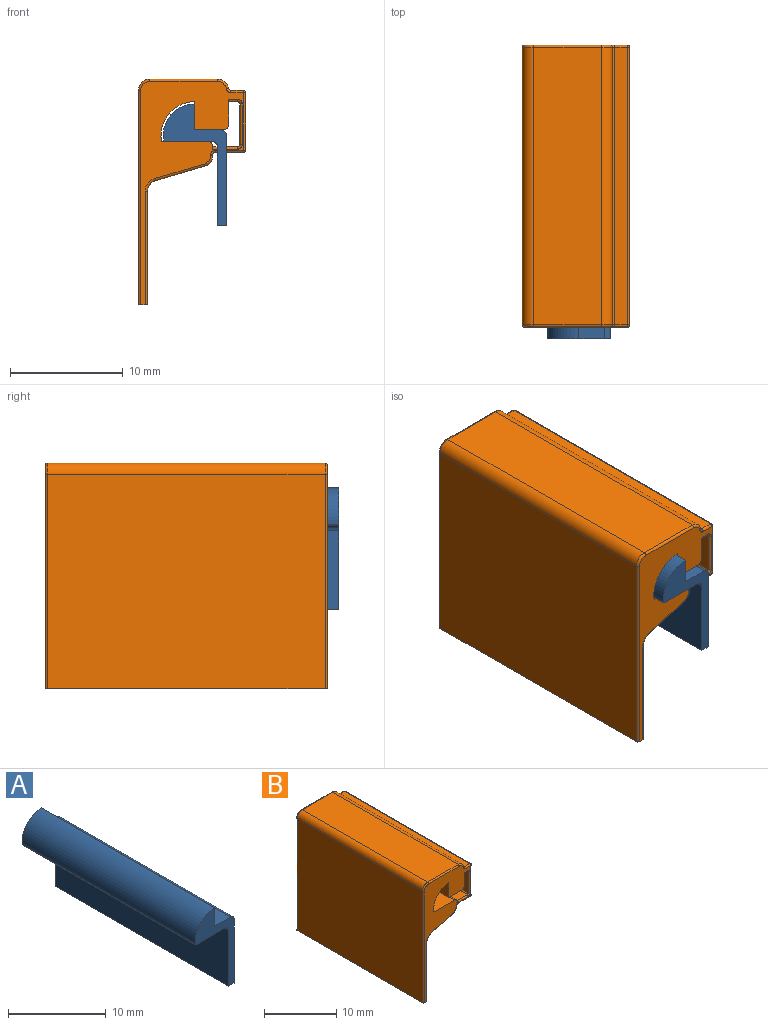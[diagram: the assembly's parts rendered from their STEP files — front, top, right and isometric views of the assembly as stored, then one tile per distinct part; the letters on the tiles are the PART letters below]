
ASSEMBLY  parts=2 mates=1
PART A: 12 faces, bbox 5.6x25x10.8 mm
  f0: plane 25x4.17mm, normal (0,0,-1), area 104.3mm2, adj f1,f9,f10,f11
  f1: cylinder r=0.5mm len=25mm, axis (0,1,0), area 19.6mm2, adj f0,f2,f10,f11
  f2: plane 25x7mm, normal (-1,0,0), area 175mm2, adj f1,f3,f10,f11
  f3: plane 25x0.8mm, normal (0,0,-1), area 20mm2, adj f2,f4,f10,f11
  f4: plane 25x8mm, normal (1,0,0), area 200mm2, adj f3,f5,f10,f11
  f5: cylinder r=0.5mm len=25mm, axis (0,1,0), area 19.6mm2, adj f4,f6,f10,f11
  f6: plane 25x2.3mm, normal (0,0,1), area 57.5mm2, adj f5,f7,f10,f11
  f7: plane 25x2.3mm, normal (1,0,0), area 57.5mm2, adj f6,f8,f10,f11
  f8: cylinder r=2.8mm len=25mm, axis (0,1,0), area 120.4mm2, adj f7,f9,f10,f11
  f9: cylinder r=0.1mm len=25mm, axis (0,1,0), area 3.6mm2, adj f0,f8,f10,f11
  f10: plane 10.8x5.6mm, normal (0,-1,0), area 16.3mm2, adj f0,f1,f2,f3,f4,f5,f6,f7
  f11: plane 10.8x5.6mm, normal (0,1,0), area 16.3mm2, adj f0,f1,f2,f3,f4,f5,f6,f7
PART B: 74 faces, bbox 9.6x25x20.1 mm
  f0: plane 25x2.2mm, normal (1,0,0), area 50mm2, adj f12,f13,f18,f24,f64,f73
  f1: plane 25x3.97mm, normal (0,0,1), area 99.3mm2, adj f2,f12,f13,f19
  f2: cylinder r=0.1mm len=25mm, axis (0,1,0), area 3.6mm2, adj f1,f3,f12,f13
  f3: cylinder r=3mm len=25mm, axis (0,1,0), area 128.2mm2, adj f2,f4,f12,f13
  f4: plane 25x2.5mm, normal (-1,0,0), area 62.5mm2, adj f3,f5,f12,f13
  f5: plane 25x2.5mm, normal (0,0,-1), area 62.5mm2, adj f4,f12,f13,f18
  f6: plane 24.6x6mm, normal (0,0,1), area 147.6mm2, adj f14,f15,f28,f33
  f7: plane 24.6x19mm, normal (-1,0,0), area 467.4mm2, adj f8,f15,f26,f29
  f8: plane 25x0.8mm, normal (0,0,-1), area 20mm2, adj f7,f9,f12,f13,f26,f29,f34,f61
  f9: plane 24.6x10.04mm, normal (1,0,0), area 247mm2, adj f8,f16,f34,f61
  f10: plane 24.6x4.37mm, normal (0.28,0,-0.96), area 112mm2, adj f16,f17,f41,f59
  f11: plane 24.6x0.05mm, normal (1,0,0), area 1.3mm2, adj f17,f48,f54,f57
  f12: plane 19.8x9.1mm, normal (0,-1,0), area 52.6mm2, adj f0,f1,f2,f3,f4,f5,f8,f18
  f13: plane 19.8x9.1mm, normal (0,1,0), area 52.6mm2, adj f0,f1,f2,f3,f4,f5,f8,f18
  f14: cylinder r=1mm len=24.6mm, axis (0,1,0), area 34.5mm2, adj f6,f30,f36,f37
  f15: cylinder r=1mm len=24.6mm, axis (0,-1,0), area 38.6mm2, adj f6,f7,f27,f31
  f16: cylinder r=1mm len=24.6mm, axis (0,-1,0), area 31.6mm2, adj f9,f10,f38,f60
  f17: cylinder r=1mm len=24.6mm, axis (0,1,0), area 31.6mm2, adj f10,f11,f45,f58
  f18: cylinder r=0.5mm len=25mm, axis (0,1,0), area 19.6mm2, adj f0,f5,f12,f13
  f19: cylinder r=0.5mm len=25mm, axis (0,1,0), area 19.7mm2, adj f1,f12,f13,f20,f62,f67
  f20: plane 24.6x2.2mm, normal (0,0,1), area 54.1mm2, adj f19,f62,f66,f67
  f21: plane 24.6x2.5mm, normal (0,0,-1), area 61.5mm2, adj f49,f50,f54,f55
  f22: plane 24.6x5.1mm, normal (1,0,0), area 125.5mm2, adj f42,f43,f50,f51
  f23: plane 24.6x1.12mm, normal (0,0,1), area 27.5mm2, adj f35,f36,f43,f44
  f24: plane 24.6x0.8mm, normal (0,0,-1), area 19.7mm2, adj f0,f64,f70,f73
  f25: plane 24.6x3.6mm, normal (-1,0,0), area 88.6mm2, adj f65,f66,f70,f71
  f26: cylinder r=0.2mm len=19mm, axis (0,0,1), area 6mm2, adj f7,f8,f12,f27
  f27: torus R=0.8mm, axis (0,-1,0), area 0.5mm2, adj f12,f15,f26,f28
  f28: cylinder r=0.2mm len=6mm, axis (1,0,0), area 1.9mm2, adj f6,f12,f27,f30
  f29: cylinder r=0.2mm len=19mm, axis (0,0,-1), area 6mm2, adj f7,f8,f13,f31
  f30: torus R=0.8mm, axis (0,-1,0), area 0.4mm2, adj f12,f14,f28,f32
  f31: torus R=0.8mm, axis (0,-1,0), area 0.5mm2, adj f13,f15,f29,f33
  f32: torus R=0.4mm, axis (0,-1,0), area 0.1mm2, adj f12,f30,f35,f36
  f33: cylinder r=0.2mm len=6mm, axis (-1,0,0), area 1.9mm2, adj f6,f13,f31,f37
  f34: cylinder r=0.2mm len=10.04mm, axis (0,0,-1), area 3.2mm2, adj f8,f9,f12,f38
  f35: cylinder r=0.2mm len=1.12mm, axis (-1,0,0), area 0.4mm2, adj f12,f23,f32,f39
  f36: cylinder r=0.2mm len=24.6mm, axis (0,1,0), area 6.9mm2, adj f14,f23,f32,f40
  f37: torus R=0.8mm, axis (0,-1,0), area 0.4mm2, adj f13,f14,f33,f40
  f38: torus R=1.2mm, axis (0,-1,0), area 0.4mm2, adj f12,f16,f34,f41
  f39: sphere r=0.2mm, area 0.1mm2, adj f35,f42,f43
  f40: torus R=0.4mm, axis (0,-1,0), area 0.1mm2, adj f13,f36,f37,f44
  f41: cylinder r=0.2mm len=4.42mm, axis (-0.96,0,-0.28), area 1.4mm2, adj f10,f12,f38,f45
  f42: cylinder r=0.2mm len=5.1mm, axis (0,0,1), area 1.6mm2, adj f12,f22,f39,f46
  f43: cylinder r=0.2mm len=24.6mm, axis (0,-1,0), area 7.7mm2, adj f22,f23,f39,f47
  f44: cylinder r=0.2mm len=1.12mm, axis (1,0,0), area 0.4mm2, adj f13,f23,f40,f47
  f45: torus R=0.8mm, axis (0,-1,0), area 0.4mm2, adj f12,f17,f41,f48
  f46: sphere r=0.2mm, area 0.1mm2, adj f42,f49,f50
  f47: sphere r=0.2mm, area 0.1mm2, adj f43,f44,f51
  f48: cylinder r=0.2mm len=0.2mm, axis (0,0,-1), area 0mm2, adj f11,f12,f45,f52
  f49: cylinder r=0.2mm len=2.5mm, axis (1,0,0), area 0.8mm2, adj f12,f21,f46,f52
  f50: cylinder r=0.2mm len=24.6mm, axis (0,1,0), area 7.7mm2, adj f21,f22,f46,f53
  f51: cylinder r=0.2mm len=5.1mm, axis (0,0,-1), area 1.6mm2, adj f13,f22,f47,f53
  f52: torus R=0.4mm, axis (0,-1,0), area 0.1mm2, adj f12,f48,f49,f54
  f53: sphere r=0.2mm, area 0.1mm2, adj f50,f51,f55
  f54: cylinder r=0.2mm len=24.6mm, axis (0,-1,0), area 7.7mm2, adj f11,f21,f52,f56
  f55: cylinder r=0.2mm len=2.5mm, axis (-1,0,0), area 0.8mm2, adj f13,f21,f53,f56
  f56: torus R=0.4mm, axis (0,-1,0), area 0.1mm2, adj f13,f54,f55,f57
  f57: cylinder r=0.2mm len=0.2mm, axis (0,0,1), area 0mm2, adj f11,f13,f56,f58
  f58: torus R=0.8mm, axis (0,-1,0), area 0.4mm2, adj f13,f17,f57,f59
  f59: cylinder r=0.2mm len=4.42mm, axis (0.96,0,0.28), area 1.4mm2, adj f10,f13,f58,f60
  f60: torus R=1.2mm, axis (0,-1,0), area 0.4mm2, adj f13,f16,f59,f61
  f61: cylinder r=0.2mm len=10.04mm, axis (0,0,1), area 3.2mm2, adj f8,f9,f13,f60
  f62: cylinder r=0.2mm len=2.24mm, axis (-1,0,0), area 0.7mm2, adj f12,f19,f20,f63
  f63: torus R=0.4mm, axis (0,-1,0), area 0.1mm2, adj f12,f62,f65,f66
  f64: cylinder r=0.2mm len=0.8mm, axis (1,0,0), area 0.3mm2, adj f0,f12,f24,f68
  f65: cylinder r=0.2mm len=3.6mm, axis (0,0,-1), area 1.1mm2, adj f12,f25,f63,f68
  f66: cylinder r=0.2mm len=24.6mm, axis (0,-1,0), area 7.7mm2, adj f20,f25,f63,f69
  f67: cylinder r=0.2mm len=2.24mm, axis (1,0,0), area 0.7mm2, adj f13,f19,f20,f69
  f68: torus R=0.4mm, axis (0,-1,0), area 0.1mm2, adj f12,f64,f65,f70
  f69: torus R=0.4mm, axis (0,-1,0), area 0.1mm2, adj f13,f66,f67,f71
  f70: cylinder r=0.2mm len=24.6mm, axis (0,1,0), area 7.7mm2, adj f24,f25,f68,f72
  f71: cylinder r=0.2mm len=3.6mm, axis (0,0,1), area 1.1mm2, adj f13,f25,f69,f72
  f72: torus R=0.4mm, axis (0,-1,0), area 0.1mm2, adj f13,f70,f71,f73
  f73: cylinder r=0.2mm len=0.8mm, axis (-1,0,0), area 0.3mm2, adj f0,f13,f24,f72
PLACE A t=(-18.08,10.81,1.87)mm
PLACE B t=(-19.27,11.82,-0.63)mm fixed
MATE slider A.f8 <-> B.f3  axis (0,-1,0) through (-18.08,-14.19,1.87)mm
